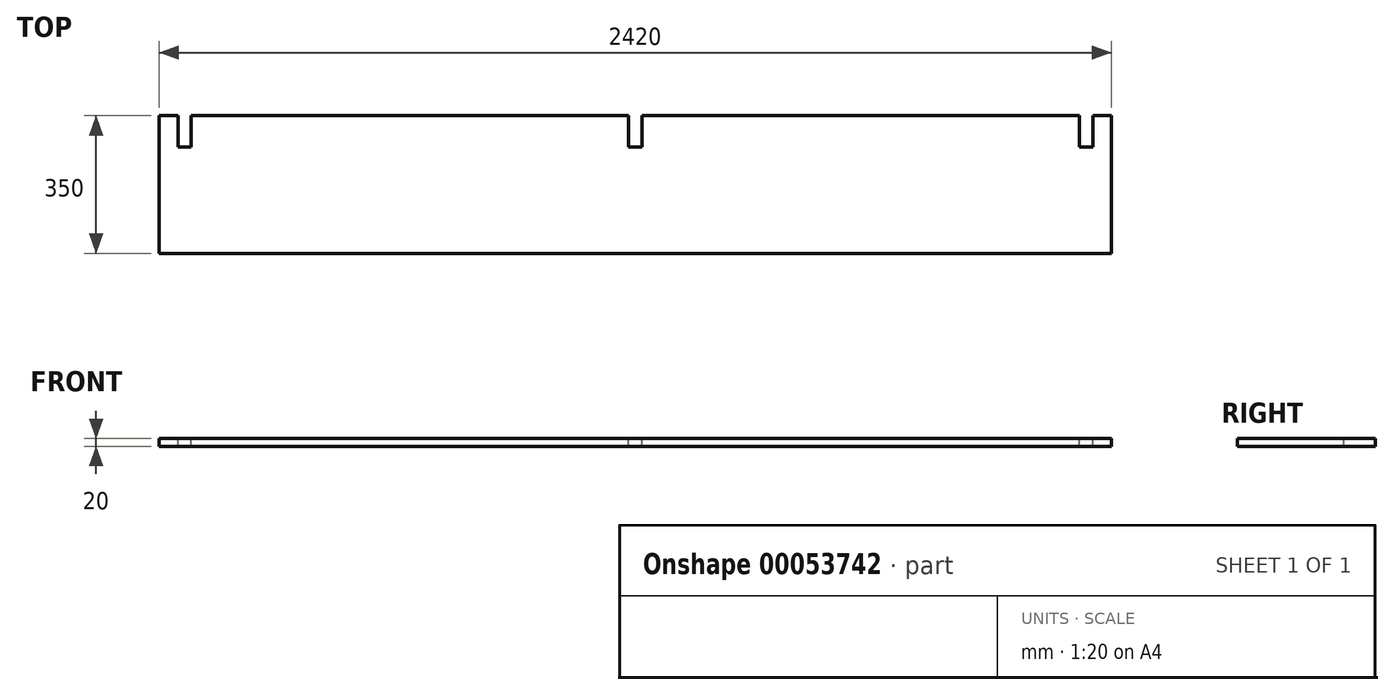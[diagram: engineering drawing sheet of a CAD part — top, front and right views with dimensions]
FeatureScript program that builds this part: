
annotation { "Feature Type Name" : "Feature", "Feature Type Description" : "" }
export const myFeature = defineFeature(function(context is Context, id is Id, definition is map)
    precondition{}
    {
        {
            var Q0;
            Q0=qCreatedBy(makeId("Top.planeOp"),FACE);
            var sketch = newSketch(context, id + "F0", { "sketchPlane" : qUnion([Q0])});
            skLineSegment(sketch, "E0.rect.bottom", {"start": v(1210, -175) * mm, "end": v(-1210, -175) * mm});
            skLineSegment(sketch, "E0.rect.top", {"start": v(1210, 175) * mm, "end": v(-1210, 175) * mm});
            skLineSegment(sketch, "E0.rect.left", {"start": v(1210, -175) * mm, "end": v(1210, 175) * mm});
            skLineSegment(sketch, "E0.rect.right", {"start": v(-1210, -175) * mm, "end": v(-1210, 175) * mm});
            skPoint(sketch, "E0.rect.middle", {"position": v(0, 0) * mm});
            skLineSegment(sketch, "E1.bottom", {"start": v(-1162, 175) * mm, "end": v(-1128, 175) * mm});
            skLineSegment(sketch, "E1.top", {"start": v(-1162, 95) * mm, "end": v(-1128, 95) * mm});
            skLineSegment(sketch, "E1.left", {"start": v(-1162, 175) * mm, "end": v(-1162, 95) * mm});
            skLineSegment(sketch, "E1.right", {"start": v(-1128, 175) * mm, "end": v(-1128, 95) * mm});
            skLineSegment(sketch, "E2.MirrorCS", {"start": v(1162, 175) * mm, "end": v(1128, 175) * mm});
            skLineSegment(sketch, "E3.MirrorCS", {"start": v(1162, 175) * mm, "end": v(1162, 95) * mm});
            skLineSegment(sketch, "E4.MirrorCS", {"start": v(1162, 95) * mm, "end": v(1128, 95) * mm});
            skLineSegment(sketch, "E5.MirrorCS", {"start": v(1128, 175) * mm, "end": v(1128, 95) * mm});
            skLineSegment(sketch, "E6.bottom", {"start": v(-17, 175) * mm, "end": v(17, 175) * mm});
            skLineSegment(sketch, "E6.top", {"start": v(-17, 95) * mm, "end": v(17, 95) * mm});
            skLineSegment(sketch, "E6.left", {"start": v(-17, 175) * mm, "end": v(-17, 95) * mm});
            skLineSegment(sketch, "E6.right", {"start": v(17, 175) * mm, "end": v(17, 95) * mm});
            skSolve(sketch);
        }
        {
            var Q0;
            Q0=qSketchRegion(id+"F0",true);
            extrude(context, id + "F1", {"entities" : qUnion([Q0]), "endBound" : BoundingType.SYMMETRIC, "depth" : 20 * mm});
        }
        {
            var Q0;
            Q0=makeQuery(id+"F1.opExtrude","CAP_FACE",FACE,{"disambiguationData":[OSD([sQuery(id+"F0.wireOp",EDGE,"E0.rect.bottom"),sQuery(id+"F0.wireOp",EDGE,"E0.rect.top"),sQuery(id+"F0.wireOp",EDGE,"E0.rect.left"),sQuery(id+"F0.wireOp",EDGE,"E0.rect.right"),sQuery(id+"F0.wireOp",EDGE,"E1.bottom"),sQuery(id+"F0.wireOp",EDGE,"E2.MirrorCS"),sQuery(id+"F0.wireOp",EDGE,"E6.bottom")])],"isStart":false});
            var sketch = newSketch(context, id + "F2", { "sketchPlane" : qUnion([Q0])});
            skLineSegment(sketch, "E7.bottom", {"start": v(-1162, 175) * mm, "end": v(-1128, 175) * mm});
            skLineSegment(sketch, "E7.top", {"start": v(-1162, 95) * mm, "end": v(-1128, 95) * mm});
            skLineSegment(sketch, "E7.left", {"start": v(-1162, 175) * mm, "end": v(-1162, 95) * mm});
            skLineSegment(sketch, "E7.right", {"start": v(-1128, 175) * mm, "end": v(-1128, 95) * mm});
            skLineSegment(sketch, "E8.bottom", {"start": v(-17, 175) * mm, "end": v(17, 175) * mm});
            skLineSegment(sketch, "E8.top", {"start": v(-17, 95) * mm, "end": v(17, 95) * mm});
            skLineSegment(sketch, "E8.left", {"start": v(-17, 175) * mm, "end": v(-17, 95) * mm});
            skLineSegment(sketch, "E8.right", {"start": v(17, 175) * mm, "end": v(17, 95) * mm});
            skLineSegment(sketch, "E9.bottom", {"start": v(1128, 175) * mm, "end": v(1162, 175) * mm});
            skLineSegment(sketch, "E9.top", {"start": v(1128, 95) * mm, "end": v(1162, 95) * mm});
            skLineSegment(sketch, "E9.left", {"start": v(1128, 175) * mm, "end": v(1128, 95) * mm});
            skLineSegment(sketch, "E9.right", {"start": v(1162, 175) * mm, "end": v(1162, 95) * mm});
            skSolve(sketch);
        }
        {
            var Q0;
            Q0 = qSketchRegion(id + "F2", true);
            extrude(context, id + "F3", {"entities" : qUnion([Q0]), "operationType" : NewBodyOperationType.REMOVE, "oppositeDirection" : true, "depth" : 25 * mm});
        }
    });
